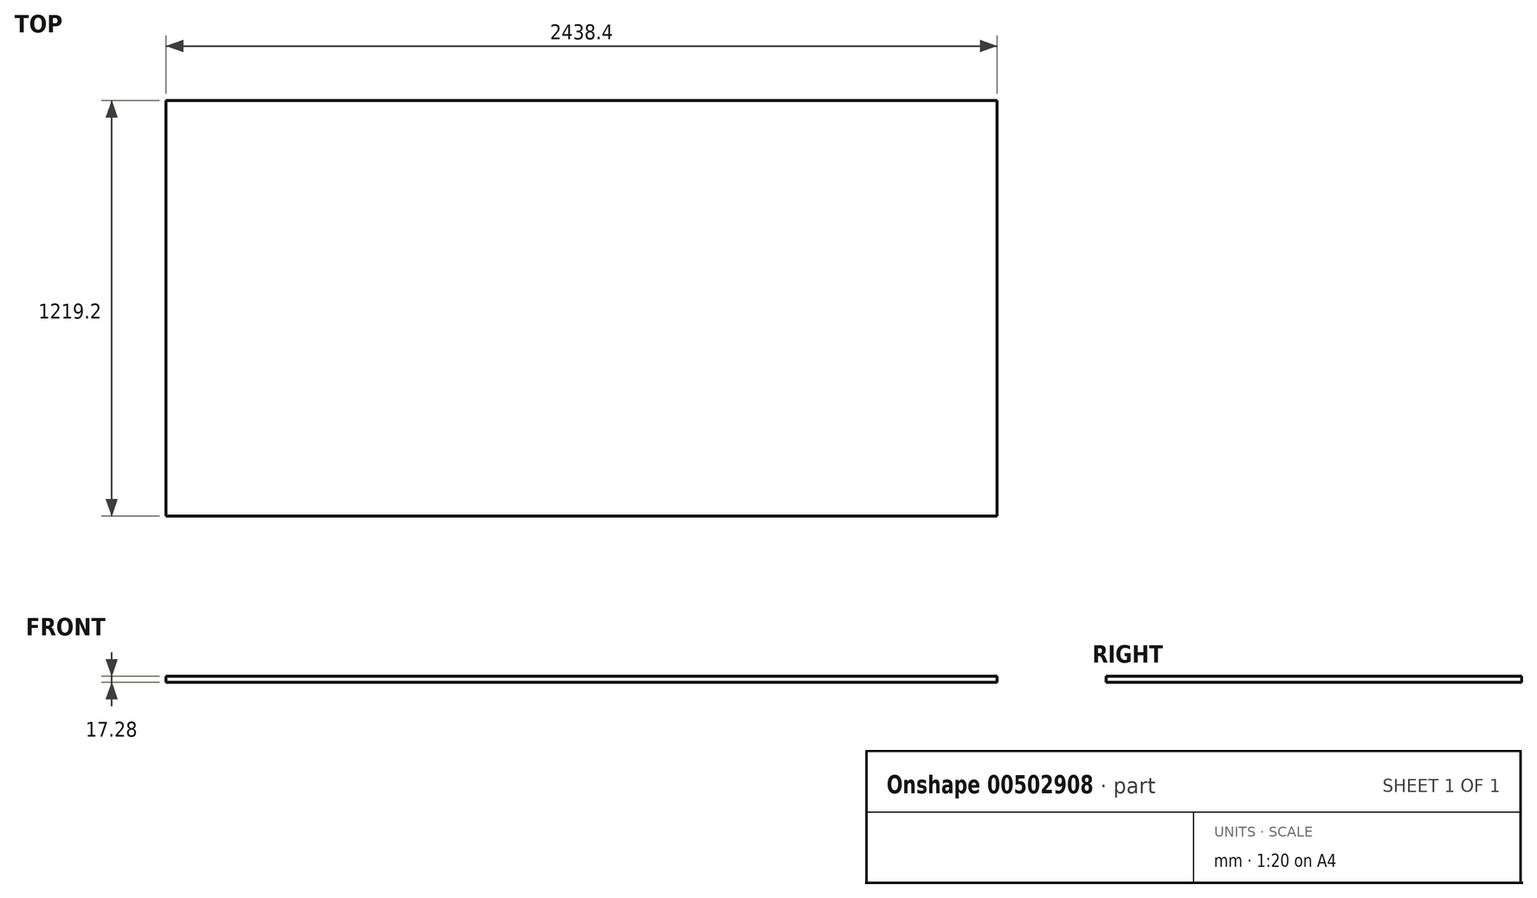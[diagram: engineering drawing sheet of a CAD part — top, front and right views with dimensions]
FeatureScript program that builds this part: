
annotation { "Feature Type Name" : "Feature", "Feature Type Description" : "" }
export const myFeature = defineFeature(function(context is Context, id is Id, definition is map)
    precondition{}
    {
        {
            var Q0;
            Q0=qCreatedBy(makeId("Top.planeOp"),FACE);
            var sketch = newSketch(context, id + "F0", { "sketchPlane" : qUnion([Q0])});
            skLineSegment(sketch, "E0.bottom", {"start": v(1219.2, -609.6) * mm, "end": v(-1219.2, -609.6) * mm});
            skLineSegment(sketch, "E0.top", {"start": v(1219.2, 609.6) * mm, "end": v(-1219.2, 609.6) * mm});
            skLineSegment(sketch, "E0.left", {"start": v(1219.2, -609.6) * mm, "end": v(1219.2, 609.6) * mm});
            skLineSegment(sketch, "E0.right", {"start": v(-1219.2, -609.6) * mm, "end": v(-1219.2, 609.6) * mm});
            skPoint(sketch, "E0.middle", {"position": v(0, 0) * mm});
            skSolve(sketch);
        }
        {
            var Q0;
            Q0=makeQuery(id+"F0.imprint","IMPRINT",FACE,{"disambiguationData":[TD([[makeQuery(id+"F0.imprint","IMPRINT",EDGE,{"derivedFrom":sQuery(id+"F0.wireOp",EDGE,"E0.bottom")}),-1.0]])]});
            extrude(context, id + "F1", {"entities" : qUnion([Q0]), "endBound" : BoundingType.SYMMETRIC, "depth" : 17.27 * mm});
        }
    });
